# Revit family: Душ для глаз аварийный настенного крепления, с чашей
name_source: partatom
category: Оборудование
revit_build: Autodesk Revit 2017 (Build: 20170118_1100(x64)
units: mm (PartAtom-declared; Revit-internal decimal feet)

## family parameters
Всегда вертикально = Да
На основе рабочей плоскости = Нет
Общий = Нет
При загрузке вырезать с полостями = Нет
Размер круглого соединителя = Использовать диаметр
Тип детали = Нормальный
Точка расчета площади = Нет

## types (1)
- Тип
    Общ_Диаметр ГВ = 13 мм
    Общ_Диаметр ХВ = 13 мм
    Общ_Единицы измерения = шт.
    Общ_Наименование = Аварийный душ для глаз настенного крепления
    Общ_Позиция = 125
    Общ_Поставщик = Delabie
    Общ_Примечание = Учтено в разделе ВК. На подводящей воду магистрали установить термостат. Под душем устроить разуклонку с трапом.
    Общ_Расход ГВ = 0.0 л/с
    Общ_Расход ХВ = 0.0 л/с
    Общ_Тип, марка = Арт. 9102
    Подключение к вентиляции = Нет
    Подключение к горячей воде = Нет
    Подключение к сливной трубе = Нет
